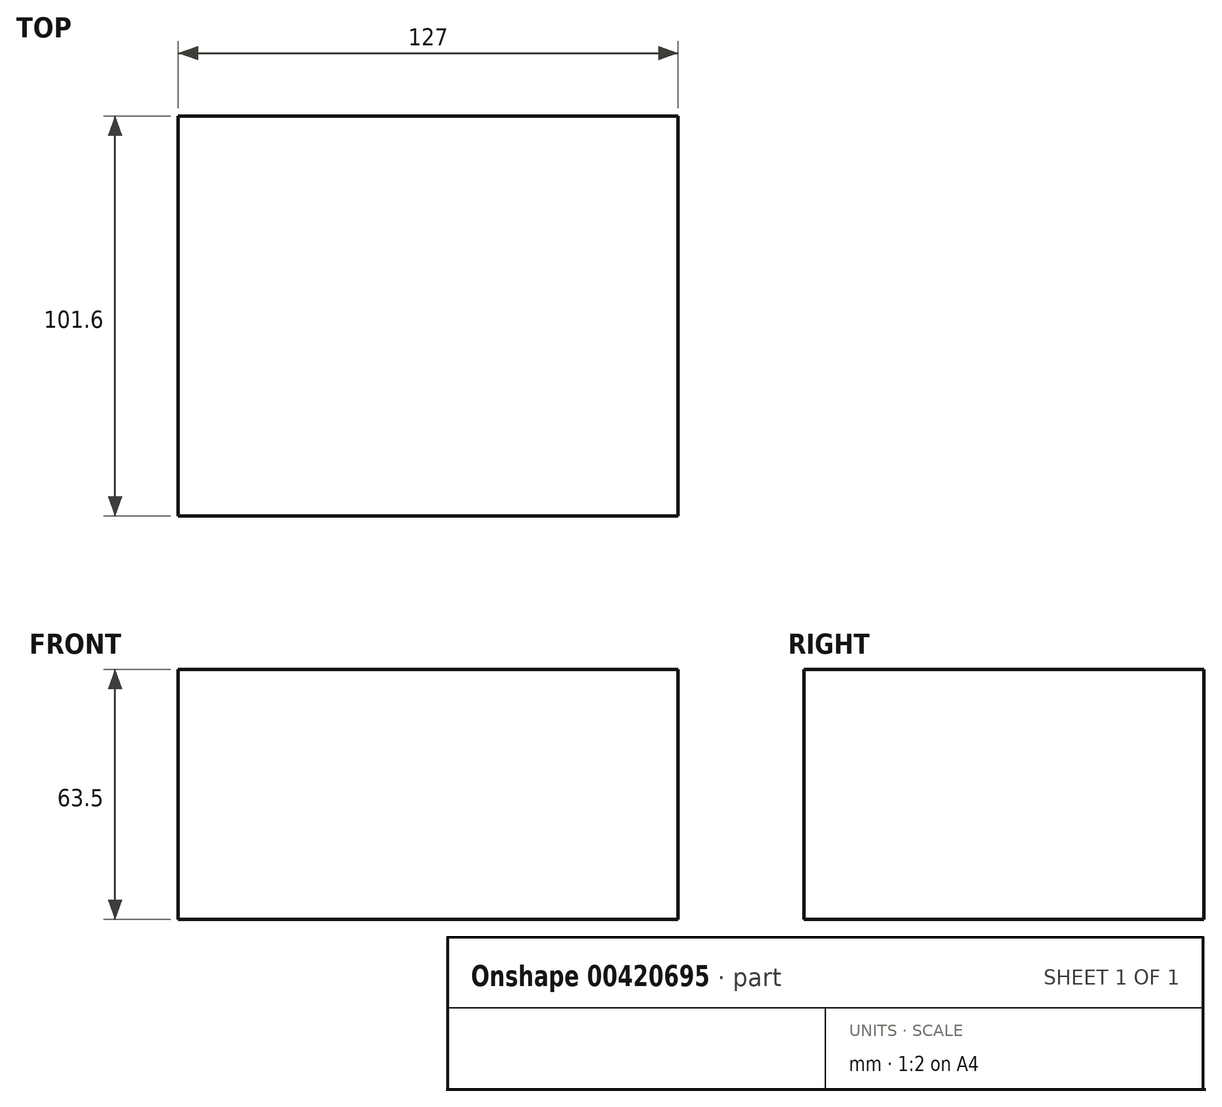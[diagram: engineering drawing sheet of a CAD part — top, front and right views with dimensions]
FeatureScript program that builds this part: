
annotation { "Feature Type Name" : "Feature", "Feature Type Description" : "" }
export const myFeature = defineFeature(function(context is Context, id is Id, definition is map)
    precondition{}
    {
        {
            var Q0;
            Q0=qCreatedBy(makeId("Front.planeOp"),FACE);
            var sketch = newSketch(context, id + "F0", { "sketchPlane" : qUnion([Q0])});
            skLineSegment(sketch, "E0.bottom", {"start": v(-63.5, 31.75) * mm, "end": v(63.5, 31.75) * mm});
            skLineSegment(sketch, "E0.top", {"start": v(-63.5, -31.75) * mm, "end": v(63.5, -31.75) * mm});
            skLineSegment(sketch, "E0.left", {"start": v(-63.5, 31.75) * mm, "end": v(-63.5, -31.75) * mm});
            skLineSegment(sketch, "E0.right", {"start": v(63.5, 31.75) * mm, "end": v(63.5, -31.75) * mm});
            skPoint(sketch, "E1", {"position": v(0, 31.75) * mm});
            skPoint(sketch, "E2", {"position": v(63.5, 0) * mm});
            skSolve(sketch);
        }
        {
            var Q0;
            Q0=makeQuery(id+"F0.imprint","IMPRINT",FACE,{"disambiguationData":[TD([[makeQuery(id+"F0.imprint","IMPRINT",EDGE,{"derivedFrom":sQuery(id+"F0.wireOp",EDGE,"E0.bottom")}),-1.0]])]});
            extrude(context, id + "F1", {"entities" : qUnion([Q0]), "endBound" : BoundingType.SYMMETRIC, "depth" : 101.6 * mm});
        }
    });
